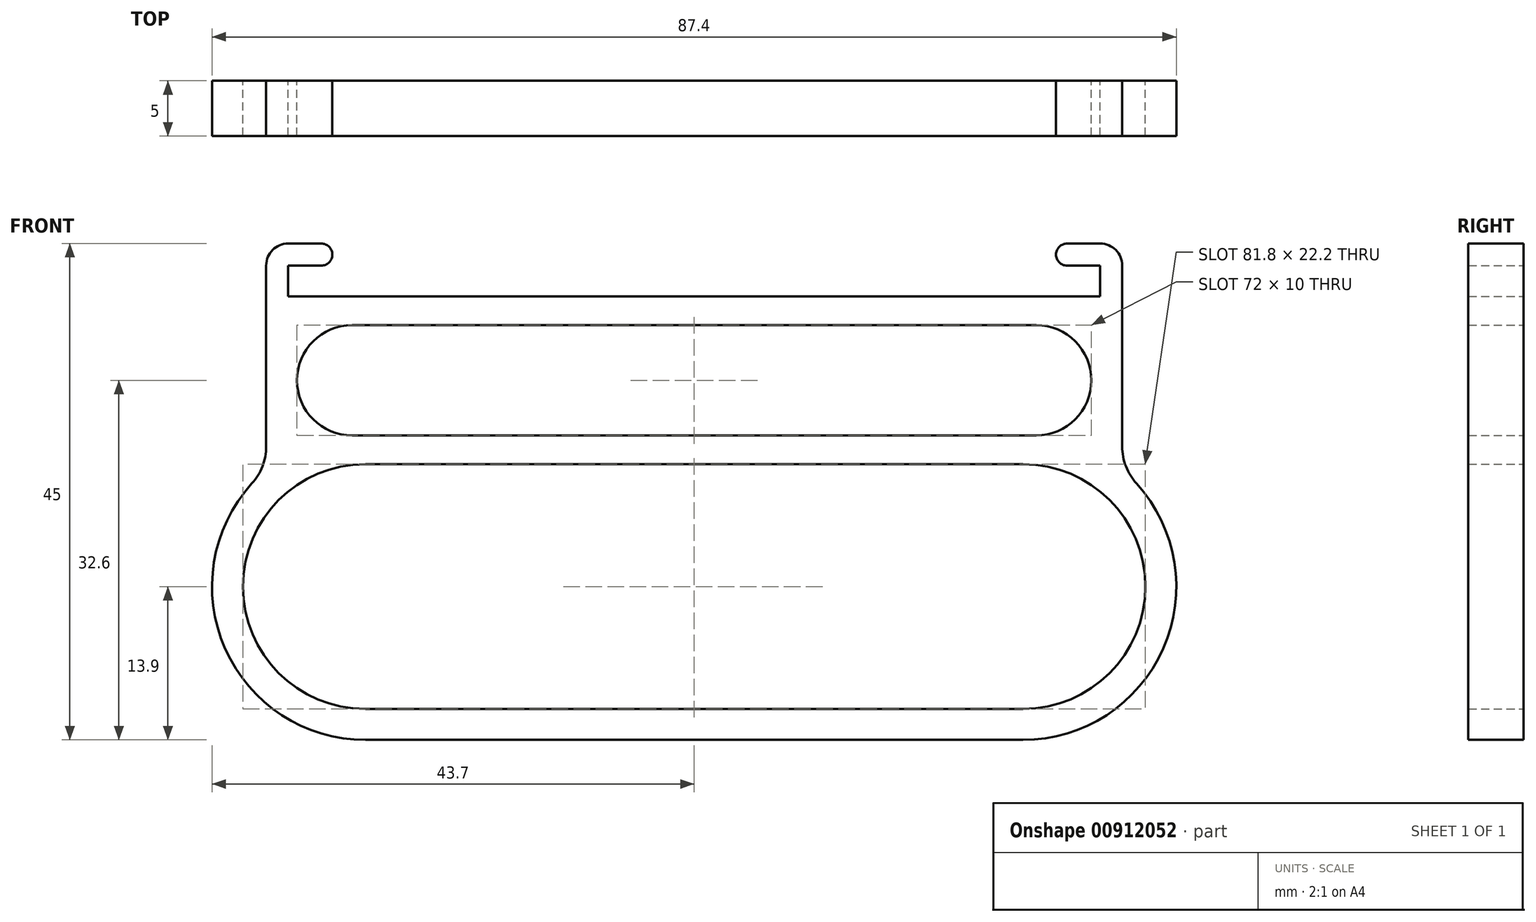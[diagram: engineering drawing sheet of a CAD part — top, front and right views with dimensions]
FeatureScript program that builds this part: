
annotation { "Feature Type Name" : "Feature", "Feature Type Description" : "" }
export const myFeature = defineFeature(function(context is Context, id is Id, definition is map)
    precondition{}
    {
        {
            var Q0;
            Q0=qCreatedBy(makeId("Front.planeOp"),FACE);
            var sketch = newSketch(context, id + "F0", { "sketchPlane" : qUnion([Q0])});
            skLineSegment(sketch, "E0.bottom", {"start": v(29.8, -11.1) * mm, "end": v(-29.8, -11.1) * mm});
            skLineSegment(sketch, "E0.top", {"start": v(29.8, 11.1) * mm, "end": v(-29.8, 11.1) * mm});
            skPoint(sketch, "E0.middle", {"position": v(0, 0) * mm});
            skArc(sketch, "E1", {"start": v(-29.8, 11.1) * mm, "mid": v(-40.9, 0) * mm, "end": v(-29.8, -11.1) * mm});
            skArc(sketch, "E2", {"start": v(29.8, -11.1) * mm, "mid": v(40.9, 0) * mm, "end": v(29.8, 11.1) * mm});
            skLineSegment(sketch, "E3.0", {"start": v(29.8, -13.9) * mm, "end": v(-29.8, -13.9) * mm});
            skArc(sketch, "E3.1", {"start": v(29.8, -13.9) * mm, "mid": v(42.5, -5.63) * mm, "end": v(40.1, 9.34) * mm});
            skArc(sketch, "E3.3", {"start": v(-40.1, 9.34) * mm, "mid": v(-42.5, -5.63) * mm, "end": v(-29.8, -13.9) * mm});
            skLineSegment(sketch, "E4.top", {"start": v(36.8, 31.1) * mm, "end": v(33.8, 31.1) * mm});
            skLineSegment(sketch, "E4.left", {"start": v(38.8, 12.7) * mm, "end": v(38.8, 29.1) * mm});
            skLineSegment(sketch, "E4.right", {"start": v(-38.8, 12.7) * mm, "end": v(-38.8, 29.1) * mm});
            skLineSegment(sketch, "E5.0", {"start": v(-36.8, 26.3) * mm, "end": v(-36.8, 29.1) * mm});
            skLineSegment(sketch, "E5.1", {"start": v(36.8, 26.3) * mm, "end": v(-36.8, 26.3) * mm});
            skLineSegment(sketch, "E5.2", {"start": v(36.8, 26.3) * mm, "end": v(36.8, 29.1) * mm});
            skLineSegment(sketch, "E5.3", {"start": v(36.8, 29.1) * mm, "end": v(33.8, 29.1) * mm});
            skLineSegment(sketch, "E6.left", {"start": v(32.8, 30.1) * mm, "end": v(32.8, 30.1) * mm});
            skLineSegment(sketch, "E6.right", {"start": v(-32.8, 30.1) * mm, "end": v(-32.8, 30.1) * mm});
            skLineSegment(sketch, "E7.trimOffspring", {"start": v(-33.8, 31.1) * mm, "end": v(-36.8, 31.1) * mm});
            skLineSegment(sketch, "E8.trimOffspring", {"start": v(-33.8, 29.1) * mm, "end": v(-36.8, 29.1) * mm});
            skPoint(sketch, "E9.visualSharp", {"position": v(-38.8, 10.6) * mm});
            skArc(sketch, "E9.filletArc", {"start": v(-40.1, 9.34) * mm, "mid": v(-39.14, 10.9) * mm, "end": v(-38.8, 12.7) * mm});
            skPoint(sketch, "E10.visualSharp", {"position": v(38.8, 10.6) * mm});
            skArc(sketch, "E10.filletArc", {"start": v(38.8, 12.7) * mm, "mid": v(39.14, 10.9) * mm, "end": v(40.1, 9.34) * mm});
            skPoint(sketch, "E11.visualSharp", {"position": v(-38.8, 31.1) * mm});
            skArc(sketch, "E11.filletArc", {"start": v(-36.8, 31.1) * mm, "mid": v(-38.21, 30.51) * mm, "end": v(-38.8, 29.1) * mm});
            skPoint(sketch, "E12.visualSharp", {"position": v(38.8, 31.1) * mm});
            skArc(sketch, "E12.filletArc", {"start": v(38.8, 29.1) * mm, "mid": v(38.21, 30.51) * mm, "end": v(36.8, 31.1) * mm});
            skPoint(sketch, "E13.visualSharp", {"position": v(-32.8, 31.1) * mm});
            skArc(sketch, "E13.filletArc", {"start": v(-32.8, 30.1) * mm, "mid": v(-33.1, 30.8) * mm, "end": v(-33.8, 31.1) * mm});
            skPoint(sketch, "E14.visualSharp", {"position": v(-32.8, 29.1) * mm});
            skArc(sketch, "E14.filletArc", {"start": v(-33.8, 29.1) * mm, "mid": v(-33.1, 29.4) * mm, "end": v(-32.8, 30.1) * mm});
            skPoint(sketch, "E15.visualSharp", {"position": v(32.8, 31.1) * mm});
            skArc(sketch, "E15.filletArc", {"start": v(33.8, 31.1) * mm, "mid": v(33.1, 30.8) * mm, "end": v(32.8, 30.1) * mm});
            skPoint(sketch, "E16.visualSharp", {"position": v(32.8, 29.1) * mm});
            skArc(sketch, "E16.filletArc", {"start": v(32.8, 30.1) * mm, "mid": v(33.1, 29.4) * mm, "end": v(33.8, 29.1) * mm});
            skLineSegment(sketch, "E17", {"start": v(-31, 23.7) * mm, "end": v(31, 23.7) * mm});
            skLineSegment(sketch, "E18", {"start": v(-31, 13.7) * mm, "end": v(31, 13.7) * mm});
            skArc(sketch, "E19", {"start": v(31, 13.7) * mm, "mid": v(36, 18.7) * mm, "end": v(31, 23.7) * mm});
            skArc(sketch, "E20", {"start": v(-31, 23.7) * mm, "mid": v(-36, 18.7) * mm, "end": v(-31, 13.7) * mm});
            skLineSegment(sketch, "E21", {"start": v(-31, 18.7) * mm, "end": v(31, 18.7) * mm, "construction": true});
            skPoint(sketch, "E22", {"position": v(0, 18.7) * mm});
            skSolve(sketch);
        }
        {
            var Q0;
            Q0=qSketchRegion(id+"F0",true);
            extrude(context, id + "F1", {"entities" : qUnion([Q0]), "depth" : 5 * mm, "offsetDistance" : 25 * mm});
        }
    });
